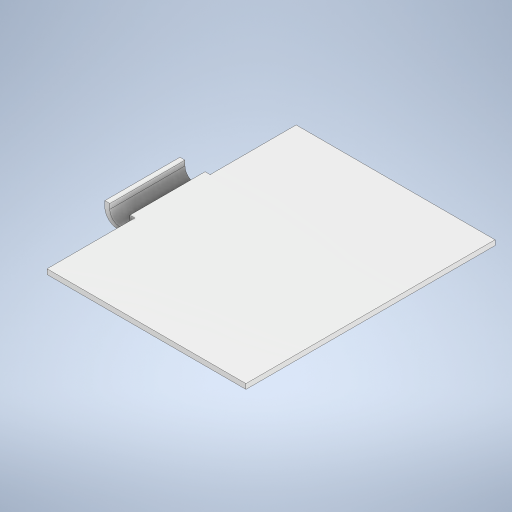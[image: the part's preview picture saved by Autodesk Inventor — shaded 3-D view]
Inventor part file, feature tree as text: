
AUTODESK INVENTOR PART (.ipt)
format: ipt  version: 2023 (Build 270158000, 158)  size: 245,248 bytes
history: native  units: in
note: dims shown in document units (in); Inventor stores cm internally (conversion verified against a paired STEP export)
features: extrude x3, sketch x2, fillet x1
ambient origin geometry x8: Origin, YZ Plane, XZ Plane, XY Plane, X Axis, Y Axis, Z Axis, Center Point
bodies: Solid1 (feature_tree)
feature tree (6):
  sketch  "Sketch1"  dims[d0=1.98in d1=2.48in]
  extrude  "Extrusion1"  Depth=2.48in
  extrude  "Extrusion2"  Depth=0.748in
  extrude  "Extrusion3"  Depth=0.875in
  fillet  "Fillet1"  Radius=0.05in
  sketch  "Sketch2"  dims[d2=0.3in d3=0.748in d4=0.875in d5=0.05in d6=0.0in d7=0.18in d8=0.0in d9=0.2in d10=0.15in d11=0.05in d12=0.1in d13=0.1in d14=0.0in d15=0.0in d16=0.125in]
